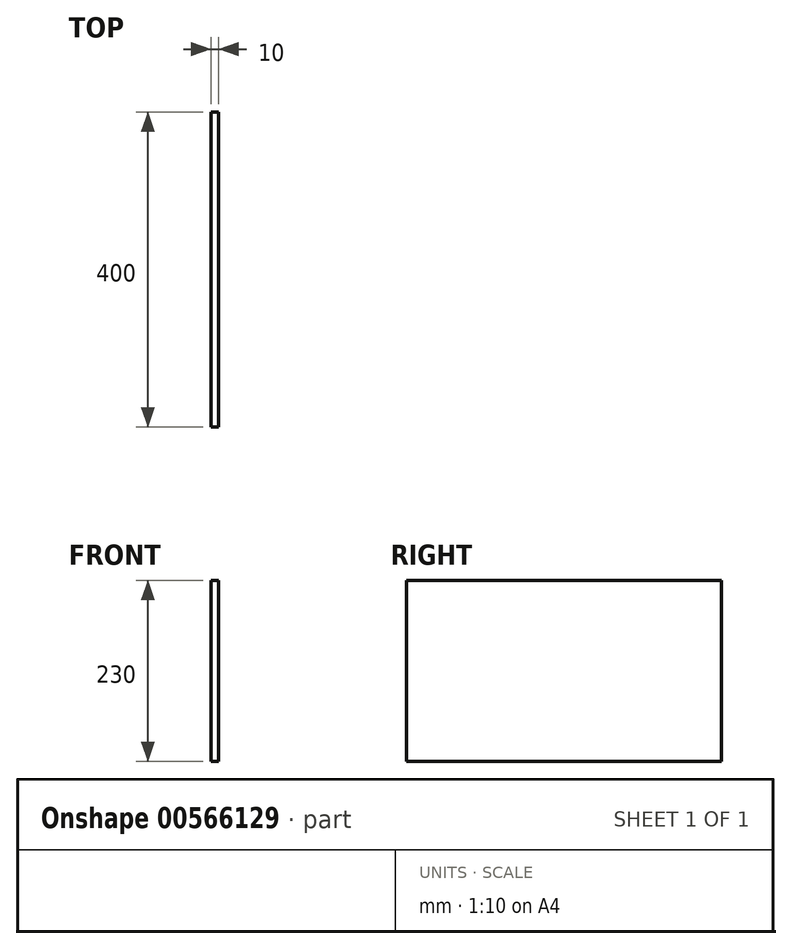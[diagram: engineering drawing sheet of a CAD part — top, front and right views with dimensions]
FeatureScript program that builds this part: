
annotation { "Feature Type Name" : "Feature", "Feature Type Description" : "" }
export const myFeature = defineFeature(function(context is Context, id is Id, definition is map)
    precondition{}
    {
        {
            var Q0;
            Q0=qCreatedBy(makeId("Front.planeOp"),FACE);
            var sketch = newSketch(context, id + "F0", { "sketchPlane" : qUnion([Q0])});
            skPoint(sketch, "E0.middle", {"position": v(0, 0) * mm});
            skLineSegment(sketch, "E1", {"start": v(-5, -180) * mm, "end": v(-5, 50) * mm});
            skLineSegment(sketch, "E2.trimOffspring", {"start": v(5, 50) * mm, "end": v(5, -180) * mm});
            skLineSegment(sketch, "E3", {"start": v(-5, 50) * mm, "end": v(5, 50) * mm});
            skLineSegment(sketch, "E4", {"start": v(5, -180) * mm, "end": v(-5, -180) * mm});
            skSolve(sketch);
        }
        {
            var Q0;
            Q0=makeQuery(id+"F0.imprint","IMPRINT",FACE,{"disambiguationData":[TD([[makeQuery(id+"F0.imprint","IMPRINT",EDGE,{"derivedFrom":sQuery(id+"F0.wireOp",EDGE,"E1")}),-1.0]])]});
            extrude(context, id + "F1", {"entities" : qUnion([Q0]), "depth" : 400 * mm, "offsetDistance" : 25 * mm});
        }
    });
